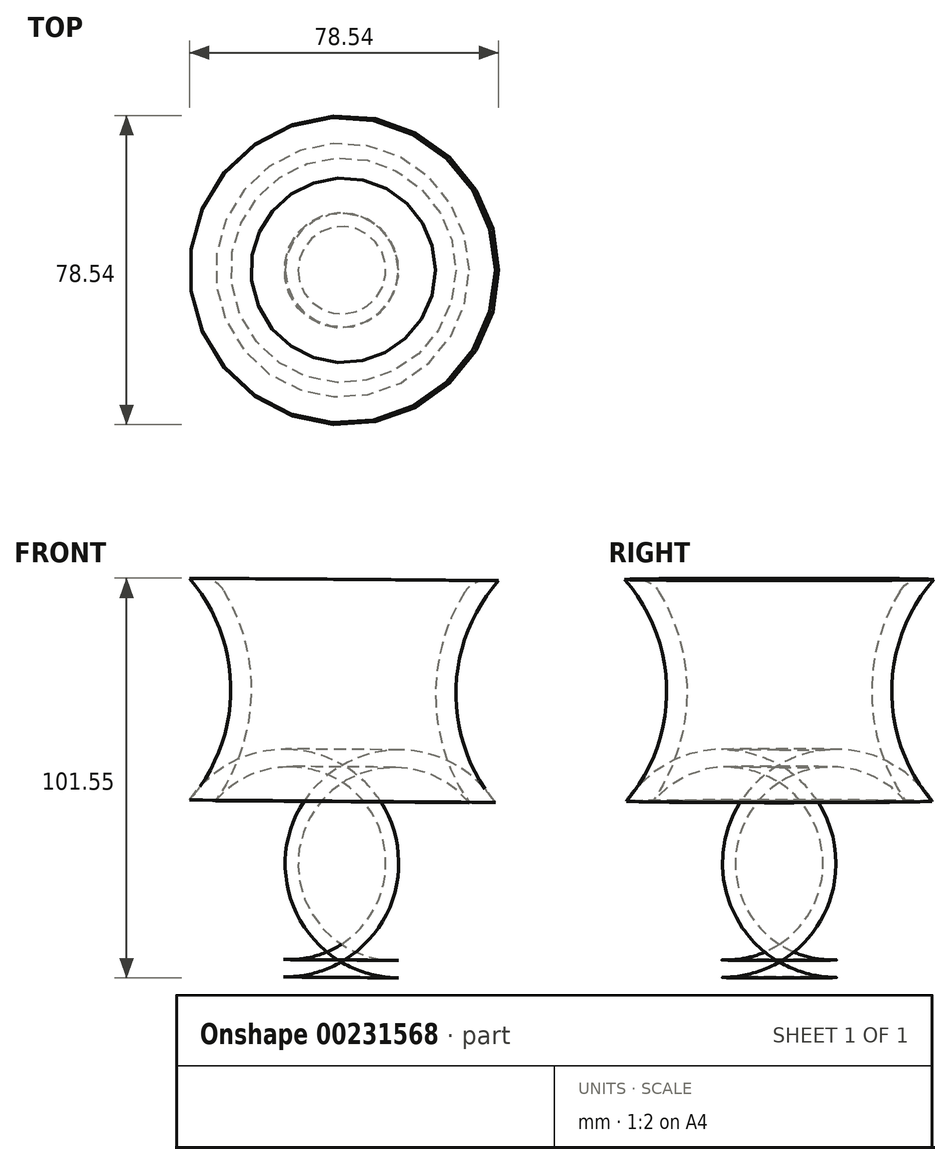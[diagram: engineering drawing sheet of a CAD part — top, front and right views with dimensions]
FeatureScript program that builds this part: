
annotation { "Feature Type Name" : "Feature", "Feature Type Description" : "" }
export const myFeature = defineFeature(function(context is Context, id is Id, definition is map)
    precondition{}
    {
        {
            var Q0;
            Q0=qCreatedBy(makeId("Front.planeOp"),FACE);
            var sketch = newSketch(context, id + "F0", { "sketchPlane" : qUnion([Q0])});
            skLineSegment(sketch, "E0", {"start": v(-35.2, 49.17) * mm, "end": v(-32.04, 49.17) * mm});
            skArc(sketch, "E1", {"start": v(-35.2, -7.18) * mm, "mid": v(-24.75, 21) * mm, "end": v(-35.2, 49.17) * mm});
            skArc(sketch, "E2", {"start": v(-35.2, -7.18) * mm, "mid": v(-36.64, -36.78) * mm, "end": v(-11.29, -52.15) * mm});
            skPoint(sketch, "E3", {"position": v(4.06, 49.17) * mm});
            skLineSegment(sketch, "E4", {"start": v(-11.29, -52.15) * mm, "end": v(3.27, -52.26) * mm});
            skLineSegment(sketch, "E5", {"start": v(3.27, -52.26) * mm, "end": v(3.27, -52.27) * mm});
            skLineSegment(sketch, "E6", {"start": v(3.27, -52.26) * mm, "end": v(3.3, -47.8) * mm});
            skPoint(sketch, "E7.orphan", {"position": v(-11.29, 49.17) * mm});
            skPoint(sketch, "E8.orphan", {"position": v(18.7, 49.17) * mm});
            skPoint(sketch, "E9.visualSharp", {"position": v(-23.25, 49.17) * mm});
            skPoint(sketch, "E10.visualSharp", {"position": v(31.01, 49.17) * mm});
            skArc(sketch, "E11", {"start": v(-28.62, -7.35) * mm, "mid": v(-19.64, 19.07) * mm, "end": v(-26.6, 46.1) * mm});
            skArc(sketch, "E12", {"start": v(-28.62, -7.35) * mm, "mid": v(-32.43, -32.88) * mm, "end": v(-11.29, -47.69) * mm});
            skLineSegment(sketch, "E13", {"start": v(-11.29, -47.69) * mm, "end": v(3.3, -47.8) * mm});
            skPoint(sketch, "E14.MirrorCS.start.orphan", {"position": v(43.33, 49.17) * mm});
            skLineSegment(sketch, "E15.MirrorCS", {"start": v(43.33, 48.55) * mm, "end": v(40.17, 48.6) * mm});
            skArc(sketch, "E16.MirrorCS", {"start": v(42.44, -7.79) * mm, "mid": v(32.43, 20.55) * mm, "end": v(43.33, 48.55) * mm});
            skArc(sketch, "E17.MirrorCS", {"start": v(35.85, -7.86) * mm, "mid": v(27.3, 18.7) * mm, "end": v(34.68, 45.6) * mm});
            skArc(sketch, "E18.MirrorCS", {"start": v(35.85, -7.86) * mm, "mid": v(39.26, -33.44) * mm, "end": v(17.9, -47.92) * mm});
            skArc(sketch, "E19.MirrorCS", {"start": v(42.44, -7.79) * mm, "mid": v(43.4, -37.41) * mm, "end": v(17.82, -52.38) * mm});
            skLineSegment(sketch, "E20.MirrorCS", {"start": v(17.9, -47.92) * mm, "end": v(3.3, -47.8) * mm});
            skLineSegment(sketch, "E21.MirrorCS", {"start": v(17.82, -52.38) * mm, "end": v(3.27, -52.26) * mm});
            skPoint(sketch, "E22.visualSharp", {"position": v(-28.62, 49.17) * mm});
            skArc(sketch, "E22.filletArc", {"start": v(-26.6, 46.1) * mm, "mid": v(-28.92, 48.34) * mm, "end": v(-32.04, 49.17) * mm});
            skPoint(sketch, "E23.visualSharp", {"position": v(36.74, 48.65) * mm});
            skArc(sketch, "E23.filletArc", {"start": v(40.17, 48.6) * mm, "mid": v(37.03, 47.83) * mm, "end": v(34.68, 45.6) * mm});
            skSolve(sketch);
        }
        {
            var Q0;
            {var subQ1=sQuery(id+"F0.wireOp",EDGE,"E0");Q0=makeQuery(id+"F0.imprint","IMPRINT",FACE,{"disambiguationData":[TD([[makeQuery(id+"F0.imprint","IMPRINT",EDGE,{"derivedFrom":subQ1}),-1.0]])]});}
            var Q1;
            Q1=sQuery(id+"F0.wireOp",EDGE,"E5");
            revolve(context, id + "F1", {"entities" : qUnion([Q0]), "axis" : qUnion([Q1]), "revolveType" : RevolveType.FULL});
        }
    });
